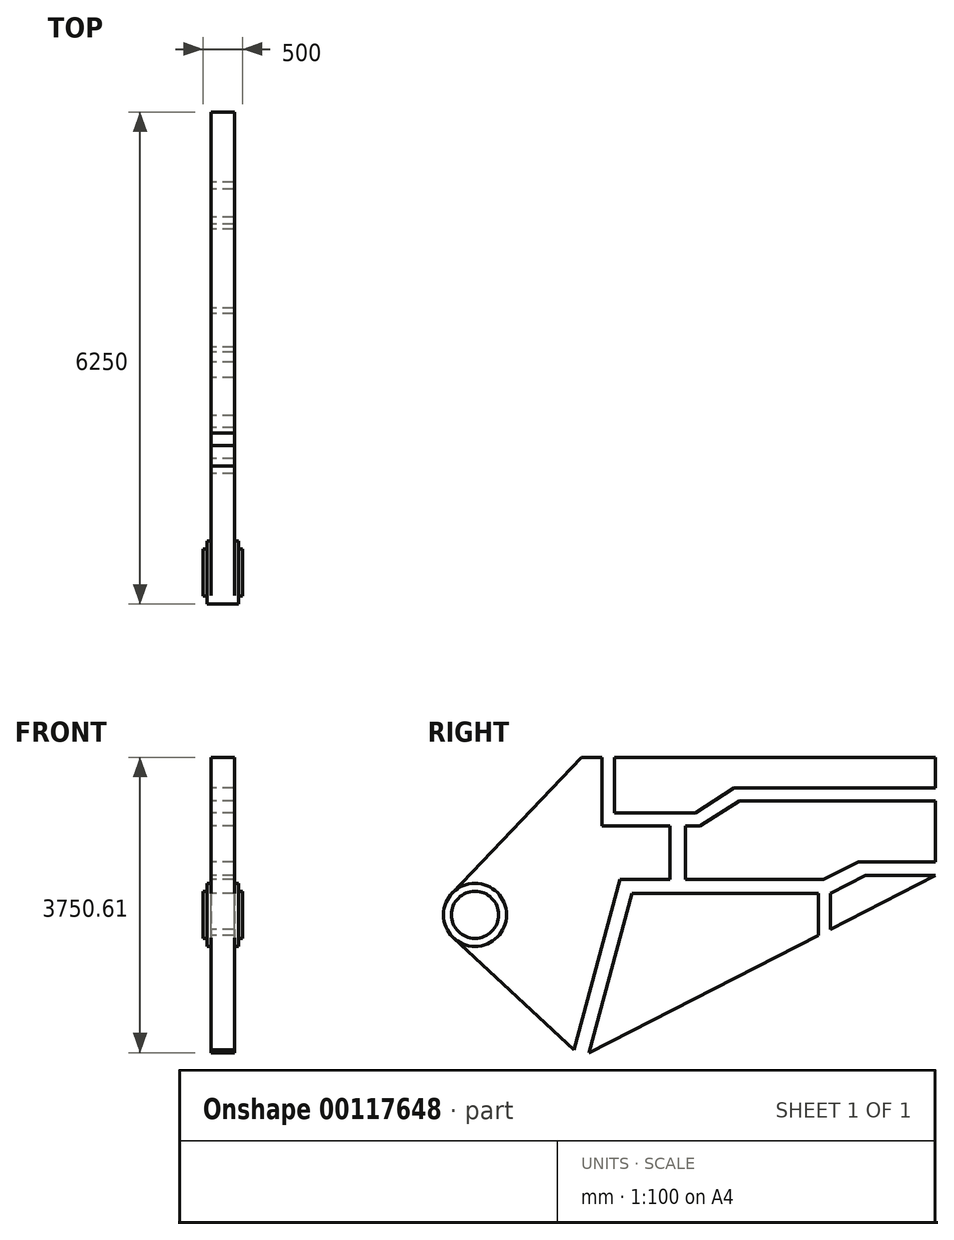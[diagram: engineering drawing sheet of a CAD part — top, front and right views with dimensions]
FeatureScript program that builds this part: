
annotation { "Feature Type Name" : "Feature", "Feature Type Description" : "" }
export const myFeature = defineFeature(function(context is Context, id is Id, definition is map)
    precondition{}
    {
        {
            var Q0;
            Q0=qCreatedBy(makeId("Right.planeOp"),FACE);
            var sketch = newSketch(context, id + "F0", { "sketchPlane" : qUnion([Q0])});
            skLineSegment(sketch, "E0.bottom", {"start": v(-3125, 1900) * mm, "end": v(3125, 1900) * mm});
            skLineSegment(sketch, "E0.top", {"start": v(-3125, -1900) * mm, "end": v(3125, -1900) * mm});
            skLineSegment(sketch, "E0.left", {"start": v(-3125, 1900) * mm, "end": v(-3125, -1900) * mm});
            skLineSegment(sketch, "E0.right", {"start": v(3125, 1900) * mm, "end": v(3125, -1900) * mm});
            skPoint(sketch, "E0.middle", {"position": v(0, 0) * mm});
            skLineSegment(sketch, "E1", {"start": v(3125, 400) * mm, "end": v(-1375, -1900) * mm});
            skLineSegment(sketch, "E2", {"start": v(3125, 1900) * mm, "end": v(3125, 400) * mm});
            skLineSegment(sketch, "E3", {"start": v(3125, 1900) * mm, "end": v(-1375, 1900) * mm});
            skCircle(sketch, "E4", {"center": v(-2725, -100) * mm, "radius": 400 * mm});
            skLineSegment(sketch, "E5", {"start": v(-1375, 1900) * mm, "end": v(-3014.85, 175.65) * mm});
            skLineSegment(sketch, "E6", {"start": v(-1375, -1900) * mm, "end": v(-2997.24, -393.07) * mm});
            skCircle(sketch, "E7", {"center": v(-2725, -100) * mm, "radius": 300 * mm});
            skLineSegment(sketch, "E8", {"start": v(-1468.24, -1813.39) * mm, "end": v(-885.13, 348.43) * mm});
            skLineSegment(sketch, "E9", {"start": v(-885.13, 348.43) * mm, "end": v(-248.22, 348.43) * mm});
            skLineSegment(sketch, "E10", {"start": v(-248.22, 348.43) * mm, "end": v(-248.22, 1028.89) * mm});
            skLineSegment(sketch, "E11", {"start": v(-248.22, 1028.89) * mm, "end": v(-1113.77, 1028.89) * mm});
            skLineSegment(sketch, "E12", {"start": v(-1113.77, 1028.89) * mm, "end": v(-1113.77, 1900) * mm});
            skLineSegment(sketch, "E13", {"start": v(-955.9, 1900) * mm, "end": v(-955.9, 1197.64) * mm});
            skLineSegment(sketch, "E14", {"start": v(-955.9, 1197.64) * mm, "end": v(72.95, 1197.64) * mm});
            skLineSegment(sketch, "E15", {"start": v(72.95, 1197.64) * mm, "end": v(562.88, 1513.38) * mm});
            skLineSegment(sketch, "E16", {"start": v(562.88, 1513.38) * mm, "end": v(3125, 1513.38) * mm});
            skLineSegment(sketch, "E17", {"start": v(3125, 1350.07) * mm, "end": v(633.65, 1350.07) * mm});
            skLineSegment(sketch, "E18", {"start": v(633.65, 1350.07) * mm, "end": v(135.27, 1028.89) * mm});
            skLineSegment(sketch, "E19", {"start": v(135.27, 1028.89) * mm, "end": v(-52.25, 1028.89) * mm});
            skLineSegment(sketch, "E20", {"start": v(-52.25, 1028.89) * mm, "end": v(-52.25, 348.43) * mm});
            skLineSegment(sketch, "E21", {"start": v(-52.25, 348.43) * mm, "end": v(1700.61, 348.43) * mm});
            skLineSegment(sketch, "E22", {"start": v(1700.61, 348.43) * mm, "end": v(2142.87, 574.47) * mm});
            skLineSegment(sketch, "E23", {"start": v(2142.87, 574.47) * mm, "end": v(3125, 574.47) * mm});
            skLineSegment(sketch, "E24", {"start": v(3125, 400) * mm, "end": v(2234.1, 400) * mm});
            skLineSegment(sketch, "E25", {"start": v(2234.1, 400) * mm, "end": v(1788.77, 172.4) * mm});
            skLineSegment(sketch, "E26", {"start": v(1788.77, 172.4) * mm, "end": v(1788.77, -282.96) * mm});
            skLineSegment(sketch, "E27", {"start": v(1634.05, -362.04) * mm, "end": v(1634.05, 172.4) * mm});
            skLineSegment(sketch, "E28", {"start": v(1634.05, 172.4) * mm, "end": v(-732.7, 172.4) * mm});
            skLineSegment(sketch, "E29", {"start": v(-732.7, 172.4) * mm, "end": v(-1278.37, -1850.61) * mm});
            skSolve(sketch);
        }
        {
            var Q0;
            Q0=makeQuery(id+"F0.imprint","IMPRINT",FACE,{"disambiguationData":[TD([[makeQuery(id+"F0.imprint","IMPRINT",EDGE,{"derivedFrom":sQuery(id+"F0.wireOp",EDGE,"E1")}),-1.0]])]});
            extrude(context, id + "F1", {"entities" : qUnion([Q0]), "depth" : 200 * mm, "symmetric" : true});
        }
        {
            var Q0;
            Q0=makeQuery(id+"F0.imprint","IMPRINT",FACE,{"disambiguationData":[TD([[makeQuery(id+"F0.imprint","IMPRINT",EDGE,{"derivedFrom":sQuery(id+"F0.wireOp",EDGE,"E7")}),-1.0]])]});
            extrude(context, id + "F2", {"entities" : qUnion([Q0]), "depth" : 400 * mm, "symmetric" : true});
        }
        {
            var Q0;
            Q0=makeQuery(id+"F0.imprint","IMPRINT",FACE,{"disambiguationData":[TD([[makeQuery(id+"F0.imprint","IMPRINT",EDGE,{"derivedFrom":sQuery(id+"F0.wireOp",EDGE,"E7")}),1.0]])]});
            extrude(context, id + "F3", {"entities" : qUnion([Q0]), "operationType" : NewBodyOperationType.ADD, "depth" : 500 * mm, "symmetric" : true});
        }
        {
            var Q0;
            {var subQ4=sQuery(id+"F0.wireOp",EDGE,"E5");Q0=makeQuery(id+"F0.imprint","IMPRINT",FACE,{"disambiguationData":[TD([[makeQuery(id+"F0.imprint","IMPRINT",EDGE,{"derivedFrom":subQ4}),1.0]])]});}
            var Q1;
            {var subQ4=sQuery(id+"F0.wireOp",EDGE,"E13");Q1=makeQuery(id+"F0.imprint","IMPRINT",FACE,{"disambiguationData":[TD([[makeQuery(id+"F0.imprint","IMPRINT",EDGE,{"derivedFrom":subQ4}),1.0]])]});}
            var Q2;
            {var subQ0=sQuery(id+"F0.wireOp",EDGE,"E17");Q2=makeQuery(id+"F0.imprint","IMPRINT",FACE,{"disambiguationData":[TD([[makeQuery(id+"F0.imprint","IMPRINT",EDGE,{"derivedFrom":subQ0}),1.0]])]});}
            var Q3;
            {var subQ0=sQuery(id+"F0.wireOp",EDGE,"E27");Q3=makeQuery(id+"F0.imprint","IMPRINT",FACE,{"disambiguationData":[TD([[makeQuery(id+"F0.imprint","IMPRINT",EDGE,{"derivedFrom":subQ0}),1.0]])]});}
            var Q4;
            {var subQ0=sQuery(id+"F0.wireOp",EDGE,"E24");Q4=makeQuery(id+"F0.imprint","IMPRINT",FACE,{"disambiguationData":[TD([[makeQuery(id+"F0.imprint","IMPRINT",EDGE,{"derivedFrom":subQ0}),1.0]])]});}
            extrude(context, id + "F4", {"entities" : qUnion([Q0, Q1, Q2, Q3, Q4]), "operationType" : NewBodyOperationType.ADD, "depth" : 300 * mm, "symmetric" : true});
        }
    });
